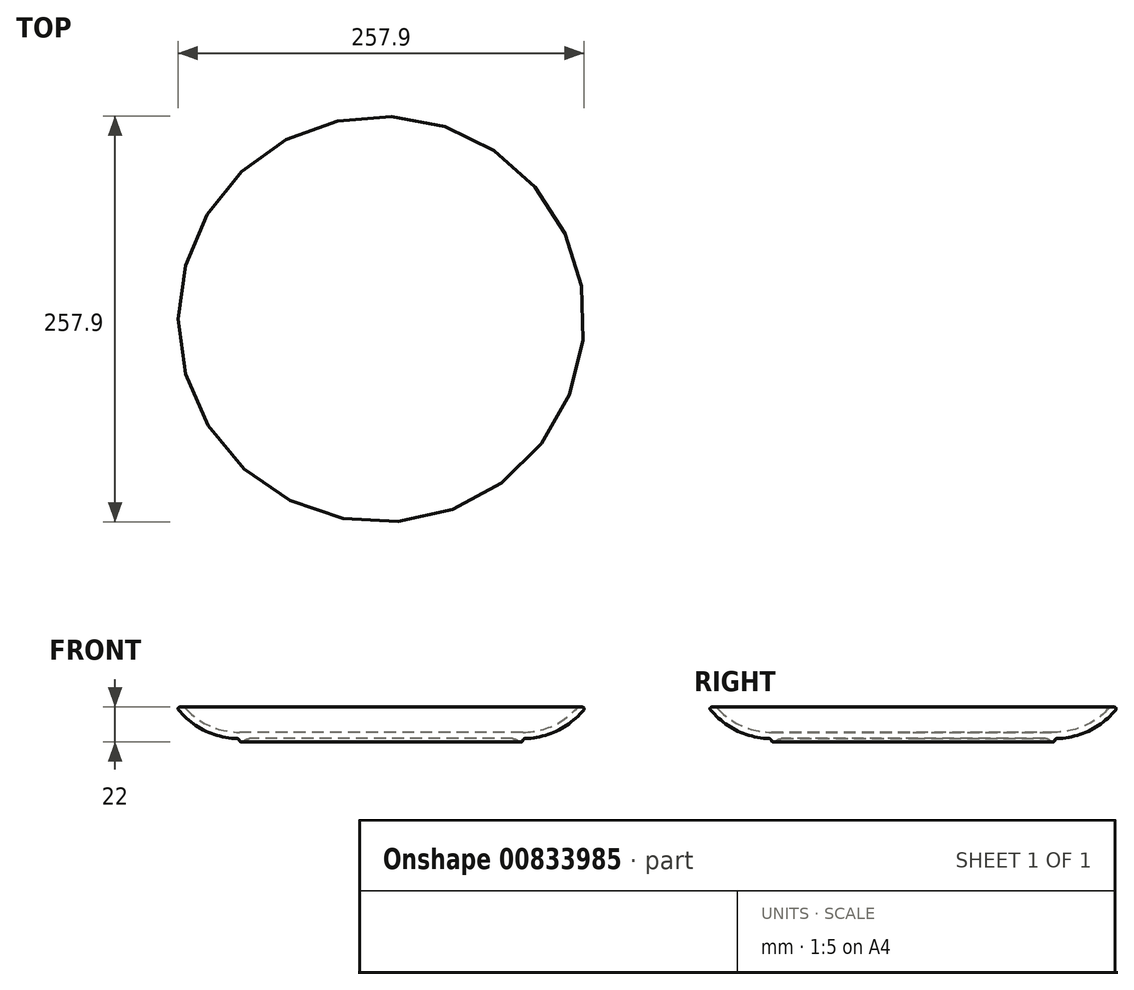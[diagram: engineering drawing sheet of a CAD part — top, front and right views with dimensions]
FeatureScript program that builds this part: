
annotation { "Feature Type Name" : "Feature", "Feature Type Description" : "" }
export const myFeature = defineFeature(function(context is Context, id is Id, definition is map)
    precondition{}
    {
        {
            var Q0;
            Q0=qCreatedBy(makeId("Front.planeOp"),FACE);
            var sketch = newSketch(context, id + "F0", { "sketchPlane" : qUnion([Q0])});
            skLineSegment(sketch, "E0", {"start": v(0, 0) * mm, "end": v(-90, 0) * mm});
            skArc(sketch, "E1", {"start": v(-130, 20) * mm, "mid": v(-112.36, 5.28) * mm, "end": v(-90, 0) * mm});
            skLineSegment(sketch, "E2.0", {"start": v(0, 4) * mm, "end": v(-90, 4) * mm});
            skArc(sketch, "E2.1", {"start": v(-124.87, 20) * mm, "mid": v(-109.18, 8.2) * mm, "end": v(-90, 4) * mm});
            skLineSegment(sketch, "E3", {"start": v(-130, 20) * mm, "end": v(-124.87, 20) * mm});
            skLineSegment(sketch, "E4", {"start": v(0, 4) * mm, "end": v(0, 0) * mm});
            skLineSegment(sketch, "E5.bottom", {"start": v(-90, 0) * mm, "end": v(-87, 0) * mm});
            skLineSegment(sketch, "E5.top", {"start": v(-90, -2) * mm, "end": v(-87, -2) * mm});
            skLineSegment(sketch, "E5.left", {"start": v(-90, 0) * mm, "end": v(-90, -2) * mm});
            skLineSegment(sketch, "E5.right", {"start": v(-87, 0) * mm, "end": v(-87, -2) * mm});
            skSolve(sketch);
        }
        {
            var Q0;
            Q0 = qSketchRegion(id + "F0", true);
            var Q1;
            Q1=sQuery(id+"F0.wireOp",EDGE,"E4");
            revolve(context, id + "F1", {"surfaceOperationType" : NewSurfaceOperationType.NEW, "entities" : qUnion([Q0]), "axis" : qUnion([Q1]), "revolveType" : RevolveType.FULL});
        }
        {
            var Q0;
            Q0=makeQuery(id+"F1.opRevolve","SWEPT_EDGE",EDGE,{"disambiguationData":[OSD([sQuery(id+"F0.wireOp",EDGE,"E1"),sQuery(id+"F0.wireOp",EDGE,"E3")])]});
            var Q1;
            Q1=makeQuery(id+"F1.opRevolve","SWEPT_EDGE",EDGE,{"disambiguationData":[OSD([sQuery(id+"F0.wireOp",EDGE,"E5.top"),sQuery(id+"F0.wireOp",EDGE,"E5.left")])]});
            var Q2;
            Q2=makeQuery(id+"F1.opRevolve","SWEPT_EDGE",EDGE,{"disambiguationData":[OSD([sQuery(id+"F0.wireOp",EDGE,"E5.top"),sQuery(id+"F0.wireOp",EDGE,"E5.right")])]});
            fillet(context, id + "F2", {"entities" : qUnion([Q0, Q1, Q2]), "radius" : 1 * mm, "tangentPropagation" : true, "allowEdgeOverflow" : false});
        }
        {
            var Q0;
            Q0=makeQuery(id+"F1.opRevolve","SWEPT_EDGE",EDGE,{"disambiguationData":[OSD([sQuery(id+"F0.wireOp",EDGE,"E2.1"),sQuery(id+"F0.wireOp",EDGE,"E3")])]});
            fillet(context, id + "F3", {"entities" : qUnion([Q0]), "radius" : 3 * mm, "tangentPropagation" : true, "allowEdgeOverflow" : false});
        }
        {
            var Q0;
            Q0=makeQuery(id+"F1.opRevolve","SWEPT_EDGE",EDGE,{"disambiguationData":[OSD([sQuery(id+"F0.wireOp",EDGE,"E1"),sQuery(id+"F0.wireOp",EDGE,"E5.bottom"),sQuery(id+"F0.wireOp",EDGE,"E5.left")])]});
            fillet(context, id + "F4", {"entities" : qUnion([Q0]), "radius" : 1.5 * mm, "tangentPropagation" : true, "allowEdgeOverflow" : false});
        }
        {
            var Q0;
            Q0=makeQuery(id+"F1.opRevolve","SWEPT_EDGE",EDGE,{"disambiguationData":[OSD([sQuery(id+"F0.wireOp",EDGE,"E0"),sQuery(id+"F0.wireOp",EDGE,"E5.bottom"),sQuery(id+"F0.wireOp",EDGE,"E5.right")])]});
            fillet(context, id + "F5", {"entities" : qUnion([Q0]), "radius" : 5 * mm, "tangentPropagation" : true, "allowEdgeOverflow" : false});
        }
    });
